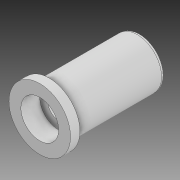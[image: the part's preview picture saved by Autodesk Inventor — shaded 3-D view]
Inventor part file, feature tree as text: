
AUTODESK INVENTOR PART (.ipt)
format: ipt  version: 2020 (Build 240168000, 168)  size: 122,880 bytes
history: native  units: mm
features: revolve x1, fillet x1, sketch x1
ambient origin geometry x8: Origin, YZ Plane, XZ Plane, XY Plane, X Axis, Y Axis, Z Axis, Center Point
bodies: Solid1 (feature_tree)
feature tree (3):
  revolve  "Revolution1"  [1 undecoded]
  fillet  "Fillet1"  Radius=1.0mm
  sketch  "Sketch1"  dims[d0=1.7mm d1=3.9mm d2=1.0mm d3=1.5mm d4=14.5mm d5=90.0deg d6=3.0mm d7=3.0mm d8=0.5mm]
note: 1 required parameter value undecoded (feature->parameter linkage not recoverable at this tier; creation-order binding heuristic only, values carry confidence <= 0.55)
